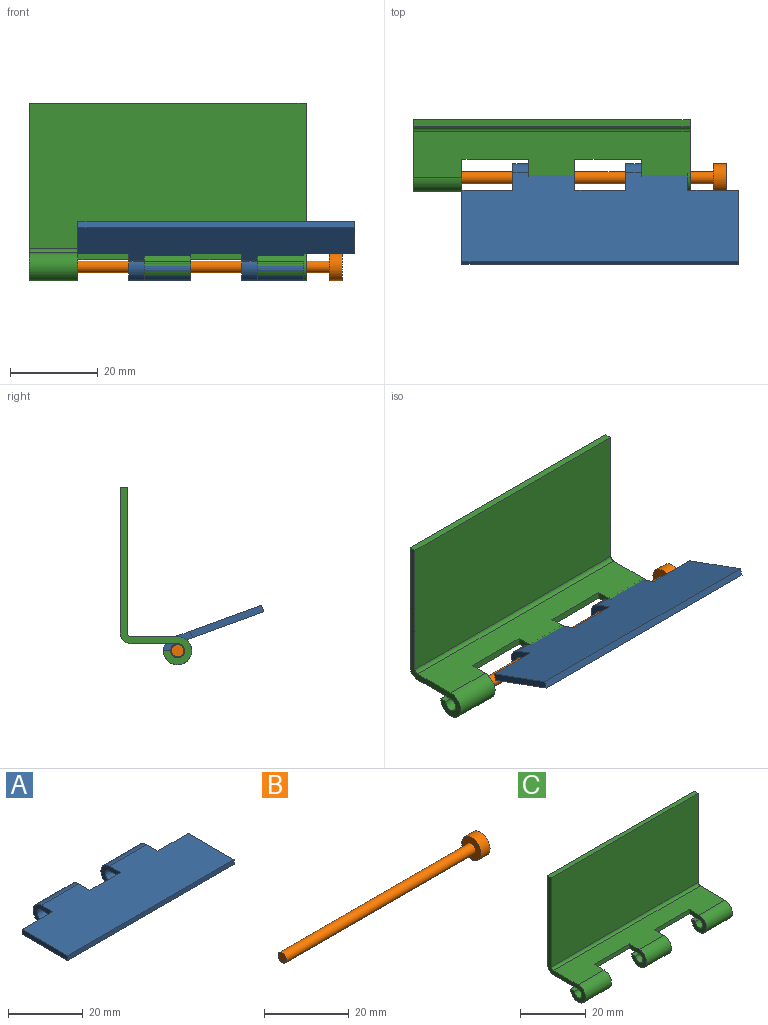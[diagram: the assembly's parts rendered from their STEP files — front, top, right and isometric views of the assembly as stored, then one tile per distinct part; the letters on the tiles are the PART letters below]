
ASSEMBLY  parts=3 mates=2
PART A: 18 faces, bbox 63x24.7x6.4 mm
  f0: plane 63x21.5mm, normal (0,0,-1), area 1208.3mm2, adj f1,f5,f6,f7,f10,f11,f12,f13
  f1: cylinder r=1.6mm len=14.1mm, axis (-1,0,0), area 106.3mm2, adj f0,f2,f11,f17
  f2: plane 14.1x1.6mm, normal (0,0,1), area 22.6mm2, adj f1,f3,f11,f17
  f3: cylinder r=3.2mm len=14.1mm, axis (-1,0,0), area 212.6mm2, adj f2,f4,f11,f17
  f4: plane 63x21.5mm, normal (0,0,1), area 1208.3mm2, adj f3,f5,f6,f9,f10,f11,f12,f13
  f5: plane 17.3x1.6mm, normal (1,0,0), area 27.7mm2, adj f0,f4,f10,f16
  f6: plane 17.3x1.6mm, normal (-1,0,0), area 27.7mm2, adj f0,f4,f10,f14
  f7: cylinder r=1.6mm len=14.1mm, axis (-1,0,0), area 106.3mm2, adj f0,f8,f12,f15
  f8: plane 14.1x1.6mm, normal (0,0,1), area 22.6mm2, adj f7,f9,f12,f15
  f9: cylinder r=3.2mm len=14.1mm, axis (-1,0,0), area 212.6mm2, adj f4,f8,f12,f15
  f10: plane 63x1.6mm, normal (0,-1,0), area 100.8mm2, adj f0,f4,f5,f6
  f11: plane 7.4x6.4mm, normal (-1,0,0), area 24.8mm2, adj f0,f1,f2,f3,f4,f13
  f12: plane 7.4x6.4mm, normal (1,0,0), area 24.8mm2, adj f0,f4,f7,f8,f9,f13
  f13: plane 11.6x1.6mm, normal (0,1,0), area 18.6mm2, adj f0,f4,f11,f12
  f14: plane 11.6x1.6mm, normal (0,1,0), area 18.6mm2, adj f0,f4,f6,f15
  f15: plane 7.4x6.4mm, normal (-1,0,0), area 24.8mm2, adj f0,f4,f7,f8,f9,f14
  f16: plane 11.6x1.6mm, normal (0,1,0), area 18.6mm2, adj f0,f4,f5,f17
  f17: plane 7.4x6.4mm, normal (1,0,0), area 24.8mm2, adj f0,f1,f2,f3,f4,f16
PART B: 5 faces, bbox 66x6.4x6.4 mm
  f0: plane 2.8x2.8mm, normal (-1,0,0), area 6.2mm2, adj f1
  f1: cylinder r=1.4mm len=63mm, axis (1,0,0), area 554.2mm2, adj f0,f4
  f2: cylinder r=3.2mm len=6.4mm, axis (-1,0,0), area 60.3mm2, adj f3,f4
  f3: plane 6.4x6.4mm, normal (1,0,0), area 32.2mm2, adj f2
  f4: plane 6.4x6.4mm, normal (-1,0,0), area 26mm2, adj f1,f2
PART C: 24 faces, bbox 63x16.3x40.4 mm
  f0: cylinder r=3.2mm len=11.1mm, axis (-1,0,0), area 167.4mm2, adj f2,f7,f8,f22
  f1: cylinder r=3.2mm len=10.6mm, axis (-1,0,0), area 159.8mm2, adj f3,f7,f18,f21
  f2: plane 11.1x1.6mm, normal (0,0,1), area 17.8mm2, adj f0,f4,f8,f22
  f3: plane 10.6x1.6mm, normal (0,0,1), area 17mm2, adj f1,f5,f18,f21
  f4: cylinder r=1.6mm len=11.1mm, axis (-1,0,0), area 83.7mm2, adj f2,f6,f8,f22
  f5: cylinder r=1.6mm len=10.6mm, axis (-1,0,0), area 79.9mm2, adj f3,f6,f18,f21
  f6: plane 63x10.6mm, normal (0,0,-1), area 541mm2, adj f4,f5,f8,f11,f12,f15,f18,f19
  f7: plane 63x10.6mm, normal (0,0,1), area 541mm2, adj f0,f1,f8,f9,f15,f17,f18,f19
  f8: plane 40.4x16.3mm, normal (1,0,0), area 92.3mm2, adj f0,f2,f4,f6,f7,f12,f13,f14
  f9: cylinder r=3.2mm len=11.1mm, axis (-1,0,0), area 167.4mm2, adj f7,f10,f15,f19
  f10: plane 11.1x1.6mm, normal (0,0,1), area 17.8mm2, adj f9,f11,f15,f19
  f11: cylinder r=1.6mm len=11.1mm, axis (-1,0,0), area 83.7mm2, adj f6,f10,f15,f19
  f12: cylinder r=2.5mm len=63mm, axis (-1,0,0), area 247.4mm2, adj f6,f8,f13,f15
  f13: plane 63x33.1mm, normal (0,1,0), area 2085.3mm2, adj f8,f12,f14,f15
  f14: plane 63x1.6mm, normal (0,0,1), area 100.8mm2, adj f8,f13,f15,f16
  f15: plane 40.4x16.3mm, normal (-1,0,0), area 92.3mm2, adj f6,f7,f9,f10,f11,f12,f13,f14
  f16: plane 63x33.1mm, normal (0,-1,0), area 2085.3mm2, adj f8,f14,f15,f17
  f17: cylinder r=0.9mm len=63mm, axis (-1,0,0), area 89.1mm2, adj f7,f8,f15,f16
  f18: plane 7.4x6.4mm, normal (-1,0,0), area 24.8mm2, adj f1,f3,f5,f6,f7,f20
  f19: plane 7.4x6.4mm, normal (1,0,0), area 24.8mm2, adj f6,f7,f9,f10,f11,f20
  f20: plane 15.1x1.6mm, normal (0,-1,0), area 24.2mm2, adj f6,f7,f18,f19
  f21: plane 7.4x6.4mm, normal (1,0,0), area 24.8mm2, adj f1,f3,f5,f6,f7,f23
  f22: plane 7.4x6.4mm, normal (-1,0,0), area 24.8mm2, adj f0,f2,f4,f6,f7,f23
  f23: plane 15.1x1.6mm, normal (0,-1,0), area 24.2mm2, adj f6,f7,f21,f22
PLACE A rot(axis=(-1,0,0),20deg) t=(-33.09,21.58,-13.14)mm
PLACE B rot(axis=(1,0,0),0deg) t=(-38.89,10.48,-12.95)mm
PLACE C t=(-44.19,10.48,-12.95)mm
MATE revolute B.f1 <-> C.f0  axis (1,0,0) through (-7.39,20.48,-16.15)mm
MATE revolute B.f1 <-> A.f1  axis (1,0,0) through (-7.39,20.48,-16.15)mm
